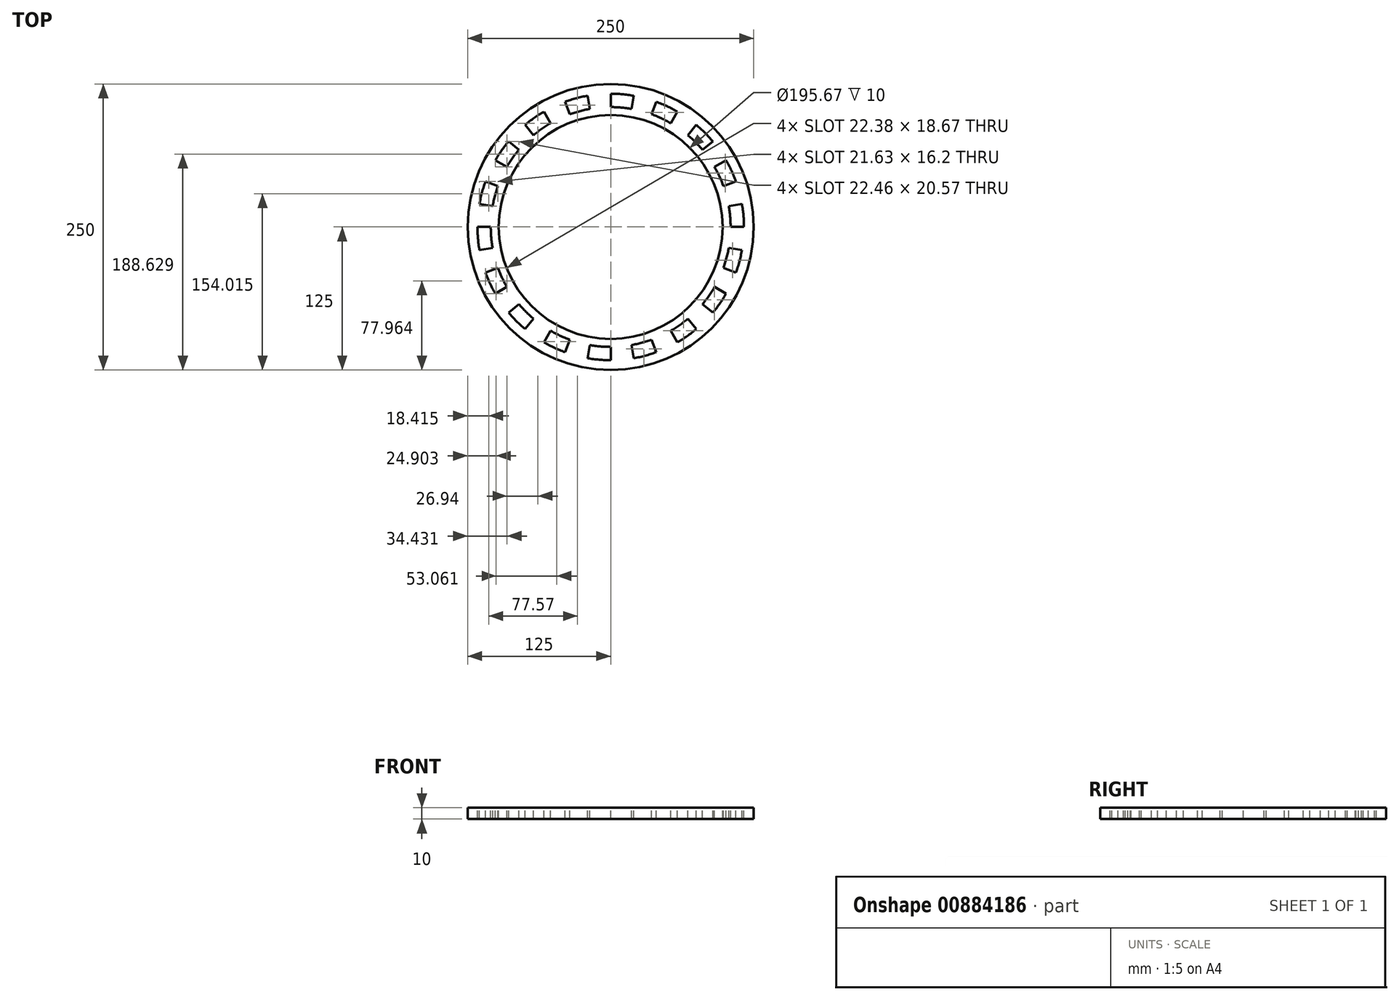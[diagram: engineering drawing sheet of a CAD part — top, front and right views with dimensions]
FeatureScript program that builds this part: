
annotation { "Feature Type Name" : "Feature", "Feature Type Description" : "" }
export const myFeature = defineFeature(function(context is Context, id is Id, definition is map)
    precondition{}
    {
        {
            var Q0;
            Q0=qCreatedBy(makeId("Top.planeOp"),FACE);
            var sketch = newSketch(context, id + "F0", { "sketchPlane" : qUnion([Q0])});
            skCircle(sketch, "E0", {"center": v(0, 0) * mm, "radius": 145 * mm});
            skArc(sketch, "E1", {"start": v(9.54, 136.41) * mm, "mid": v(4.77, 136.66) * mm, "end": v(0, 136.75) * mm});
            skArc(sketch, "E2", {"start": v(8, 114.55) * mm, "mid": v(4, 114.76) * mm, "end": v(0, 114.83) * mm});
            skLineSegment(sketch, "E3", {"start": v(0, 0) * mm, "end": v(0, 38.61) * mm, "construction": true});
            skLineSegment(sketch, "E4", {"start": v(0, 38.61) * mm, "end": v(0, 0) * mm, "construction": true});
            skLineSegment(sketch, "E5", {"start": v(0, 0) * mm, "end": v(-47.77, 0) * mm, "construction": true});
            skLineSegment(sketch, "E6", {"start": v(0, 30) * mm, "end": v(-10, 30) * mm});
            skLineSegment(sketch, "E7", {"start": v(-10, 30) * mm, "end": v(-10, 10) * mm});
            skLineSegment(sketch, "E8", {"start": v(-10, 10) * mm, "end": v(-30, 10) * mm});
            skLineSegment(sketch, "E9", {"start": v(-30, 10) * mm, "end": v(-30, 0) * mm});
            skLineSegment(sketch, "E10.MirrorCS", {"start": v(-30, -10) * mm, "end": v(-30, 0) * mm});
            skLineSegment(sketch, "E11.MirrorCS", {"start": v(-10, -10) * mm, "end": v(-30, -10) * mm});
            skLineSegment(sketch, "E12.MirrorCS", {"start": v(-10, -30) * mm, "end": v(-10, -10) * mm});
            skLineSegment(sketch, "E13.MirrorCS", {"start": v(0, -30) * mm, "end": v(-10, -30) * mm});
            skLineSegment(sketch, "E14.MirrorCS", {"start": v(0, 30) * mm, "end": v(10, 30) * mm});
            skLineSegment(sketch, "E15.MirrorCS", {"start": v(10, 30) * mm, "end": v(10, 10) * mm});
            skLineSegment(sketch, "E16.MirrorCS", {"start": v(10, 10) * mm, "end": v(30, 10) * mm});
            skLineSegment(sketch, "E17.MirrorCS", {"start": v(30, 10) * mm, "end": v(30, 0) * mm});
            skLineSegment(sketch, "E18.MirrorCS", {"start": v(30, -10) * mm, "end": v(30, 0) * mm});
            skLineSegment(sketch, "E19.MirrorCS", {"start": v(10, -10) * mm, "end": v(30, -10) * mm});
            skLineSegment(sketch, "E20.MirrorCS", {"start": v(0, -30) * mm, "end": v(10, -30) * mm});
            skLineSegment(sketch, "E21.MirrorCS", {"start": v(10, -30) * mm, "end": v(10, -10) * mm});
            skLineSegment(sketch, "E22", {"start": v(0, 114.83) * mm, "end": v(0, 136.75) * mm});
            skLineSegment(sketch, "E23", {"start": v(8, 114.55) * mm, "end": v(9.54, 136.41) * mm});
            skArc(sketch, "E24.1.0", {"start": v(-10, 114.4) * mm, "mid": v(-14, 113.98) * mm, "end": v(-17.96, 113.42) * mm});
            skLineSegment(sketch, "E24.1.1", {"start": v(-17.96, 113.42) * mm, "end": v(-21.4, 135.06) * mm});
            skArc(sketch, "E24.1.2", {"start": v(-11.92, 136.23) * mm, "mid": v(-16.67, 135.73) * mm, "end": v(-21.4, 135.06) * mm});
            skLineSegment(sketch, "E24.1.3", {"start": v(-10, 114.4) * mm, "end": v(-11.92, 136.23) * mm});
            skArc(sketch, "E24.2.0", {"start": v(-27.78, 111.42) * mm, "mid": v(-31.65, 110.39) * mm, "end": v(-35.49, 109.21) * mm});
            skLineSegment(sketch, "E24.2.1", {"start": v(-35.49, 109.21) * mm, "end": v(-42.26, 130.05) * mm});
            skArc(sketch, "E24.2.2", {"start": v(-33.08, 132.68) * mm, "mid": v(-37.7, 131.45) * mm, "end": v(-42.26, 130.05) * mm});
            skLineSegment(sketch, "E24.2.3", {"start": v(-27.78, 111.42) * mm, "end": v(-33.08, 132.68) * mm});
            skArc(sketch, "E24.3.0", {"start": v(-44.87, 105.7) * mm, "mid": v(-48.53, 104.07) * mm, "end": v(-52.13, 102.32) * mm});
            skLineSegment(sketch, "E24.3.1", {"start": v(-52.13, 102.32) * mm, "end": v(-62.08, 121.84) * mm});
            skArc(sketch, "E24.3.2", {"start": v(-53.43, 125.88) * mm, "mid": v(-57.8, 123.93) * mm, "end": v(-62.08, 121.84) * mm});
            skLineSegment(sketch, "E24.3.3", {"start": v(-44.87, 105.7) * mm, "end": v(-53.43, 125.88) * mm});
            skArc(sketch, "E24.4.0", {"start": v(-60.85, 97.38) * mm, "mid": v(-64.21, 95.2) * mm, "end": v(-67.5, 92.9) * mm});
            skLineSegment(sketch, "E24.4.1", {"start": v(-67.5, 92.9) * mm, "end": v(-80.38, 110.63) * mm});
            skArc(sketch, "E24.4.2", {"start": v(-72.47, 115.97) * mm, "mid": v(-76.47, 113.37) * mm, "end": v(-80.38, 110.63) * mm});
            skLineSegment(sketch, "E24.4.3", {"start": v(-60.85, 97.38) * mm, "end": v(-72.47, 115.97) * mm});
            skArc(sketch, "E24.5.0", {"start": v(-75.34, 86.67) * mm, "mid": v(-78.32, 83.98) * mm, "end": v(-81.2, 81.2) * mm});
            skLineSegment(sketch, "E24.5.1", {"start": v(-81.2, 81.2) * mm, "end": v(-96.7, 96.7) * mm});
            skArc(sketch, "E24.5.2", {"start": v(-89.71, 103.2) * mm, "mid": v(-93.26, 100.01) * mm, "end": v(-96.7, 96.7) * mm});
            skLineSegment(sketch, "E24.5.3", {"start": v(-75.34, 86.67) * mm, "end": v(-89.71, 103.2) * mm});
            skArc(sketch, "E24.6.0", {"start": v(-87.97, 73.81) * mm, "mid": v(-90.5, 70.7) * mm, "end": v(-92.9, 67.5) * mm});
            skLineSegment(sketch, "E24.6.1", {"start": v(-92.9, 67.5) * mm, "end": v(-110.63, 80.38) * mm});
            skArc(sketch, "E24.6.2", {"start": v(-104.75, 87.9) * mm, "mid": v(-107.76, 84.19) * mm, "end": v(-110.63, 80.38) * mm});
            skLineSegment(sketch, "E24.6.3", {"start": v(-87.97, 73.81) * mm, "end": v(-104.75, 87.9) * mm});
            skArc(sketch, "E24.7.0", {"start": v(-98.43, 59.14) * mm, "mid": v(-100.44, 55.67) * mm, "end": v(-102.32, 52.13) * mm});
            skLineSegment(sketch, "E24.7.1", {"start": v(-102.32, 52.13) * mm, "end": v(-121.84, 62.08) * mm});
            skArc(sketch, "E24.7.2", {"start": v(-117.22, 70.43) * mm, "mid": v(-119.6, 66.3) * mm, "end": v(-121.84, 62.08) * mm});
            skLineSegment(sketch, "E24.7.3", {"start": v(-98.43, 59.14) * mm, "end": v(-117.22, 70.43) * mm});
            skArc(sketch, "E24.8.0", {"start": v(-106.47, 43.02) * mm, "mid": v(-107.9, 39.28) * mm, "end": v(-109.21, 35.49) * mm});
            skLineSegment(sketch, "E24.8.1", {"start": v(-109.21, 35.49) * mm, "end": v(-130.05, 42.26) * mm});
            skArc(sketch, "E24.8.2", {"start": v(-126.79, 51.23) * mm, "mid": v(-128.5, 46.77) * mm, "end": v(-130.05, 42.26) * mm});
            skLineSegment(sketch, "E24.8.3", {"start": v(-106.47, 43.02) * mm, "end": v(-126.79, 51.23) * mm});
            skArc(sketch, "E24.9.0", {"start": v(-111.9, 25.83) * mm, "mid": v(-112.72, 21.91) * mm, "end": v(-113.42, 17.96) * mm});
            skLineSegment(sketch, "E24.9.1", {"start": v(-113.42, 17.96) * mm, "end": v(-135.06, 21.4) * mm});
            skArc(sketch, "E24.9.2", {"start": v(-133.24, 30.76) * mm, "mid": v(-134.23, 26.1) * mm, "end": v(-135.06, 21.4) * mm});
            skLineSegment(sketch, "E24.9.3", {"start": v(-111.9, 25.83) * mm, "end": v(-133.24, 30.76) * mm});
            skArc(sketch, "E24.10.0", {"start": v(-114.55, 8) * mm, "mid": v(-114.76, 4) * mm, "end": v(-114.83, 0) * mm});
            skLineSegment(sketch, "E24.10.1", {"start": v(-114.83, 0) * mm, "end": v(-136.75, 0) * mm});
            skArc(sketch, "E24.10.2", {"start": v(-136.41, 9.54) * mm, "mid": v(-136.66, 4.77) * mm, "end": v(-136.75, 0) * mm});
            skLineSegment(sketch, "E24.10.3", {"start": v(-114.55, 8) * mm, "end": v(-136.41, 9.54) * mm});
            skArc(sketch, "E24.11.0", {"start": v(-114.4, -10) * mm, "mid": v(-113.98, -14) * mm, "end": v(-113.42, -17.96) * mm});
            skLineSegment(sketch, "E24.11.1", {"start": v(-113.42, -17.96) * mm, "end": v(-135.06, -21.4) * mm});
            skArc(sketch, "E24.11.2", {"start": v(-136.23, -11.92) * mm, "mid": v(-135.73, -16.67) * mm, "end": v(-135.06, -21.4) * mm});
            skLineSegment(sketch, "E24.11.3", {"start": v(-114.4, -10) * mm, "end": v(-136.23, -11.92) * mm});
            skArc(sketch, "E24.12.0", {"start": v(-111.42, -27.78) * mm, "mid": v(-110.39, -31.65) * mm, "end": v(-109.21, -35.49) * mm});
            skLineSegment(sketch, "E24.12.1", {"start": v(-109.21, -35.49) * mm, "end": v(-130.05, -42.26) * mm});
            skArc(sketch, "E24.12.2", {"start": v(-132.68, -33.08) * mm, "mid": v(-131.45, -37.7) * mm, "end": v(-130.05, -42.26) * mm});
            skLineSegment(sketch, "E24.12.3", {"start": v(-111.42, -27.78) * mm, "end": v(-132.68, -33.08) * mm});
            skArc(sketch, "E24.13.0", {"start": v(-105.7, -44.87) * mm, "mid": v(-104.07, -48.53) * mm, "end": v(-102.32, -52.13) * mm});
            skLineSegment(sketch, "E24.13.1", {"start": v(-102.32, -52.13) * mm, "end": v(-121.84, -62.08) * mm});
            skArc(sketch, "E24.13.2", {"start": v(-125.88, -53.43) * mm, "mid": v(-123.93, -57.8) * mm, "end": v(-121.84, -62.08) * mm});
            skLineSegment(sketch, "E24.13.3", {"start": v(-105.7, -44.87) * mm, "end": v(-125.88, -53.43) * mm});
            skArc(sketch, "E24.14.0", {"start": v(-97.38, -60.85) * mm, "mid": v(-95.2, -64.21) * mm, "end": v(-92.9, -67.5) * mm});
            skLineSegment(sketch, "E24.14.1", {"start": v(-92.9, -67.5) * mm, "end": v(-110.63, -80.38) * mm});
            skArc(sketch, "E24.14.2", {"start": v(-115.97, -72.47) * mm, "mid": v(-113.37, -76.47) * mm, "end": v(-110.63, -80.38) * mm});
            skLineSegment(sketch, "E24.14.3", {"start": v(-97.38, -60.85) * mm, "end": v(-115.97, -72.47) * mm});
            skArc(sketch, "E24.15.0", {"start": v(-86.67, -75.34) * mm, "mid": v(-83.98, -78.32) * mm, "end": v(-81.2, -81.2) * mm});
            skLineSegment(sketch, "E24.15.1", {"start": v(-81.2, -81.2) * mm, "end": v(-96.7, -96.7) * mm});
            skArc(sketch, "E24.15.2", {"start": v(-103.2, -89.71) * mm, "mid": v(-100.01, -93.26) * mm, "end": v(-96.7, -96.7) * mm});
            skLineSegment(sketch, "E24.15.3", {"start": v(-86.67, -75.34) * mm, "end": v(-103.2, -89.71) * mm});
            skArc(sketch, "E24.16.0", {"start": v(-73.81, -87.97) * mm, "mid": v(-70.7, -90.5) * mm, "end": v(-67.5, -92.9) * mm});
            skLineSegment(sketch, "E24.16.1", {"start": v(-67.5, -92.9) * mm, "end": v(-80.38, -110.63) * mm});
            skArc(sketch, "E24.16.2", {"start": v(-87.9, -104.75) * mm, "mid": v(-84.19, -107.76) * mm, "end": v(-80.38, -110.63) * mm});
            skLineSegment(sketch, "E24.16.3", {"start": v(-73.81, -87.97) * mm, "end": v(-87.9, -104.75) * mm});
            skArc(sketch, "E24.17.0", {"start": v(-59.14, -98.43) * mm, "mid": v(-55.67, -100.44) * mm, "end": v(-52.13, -102.32) * mm});
            skLineSegment(sketch, "E24.17.1", {"start": v(-52.13, -102.32) * mm, "end": v(-62.08, -121.84) * mm});
            skArc(sketch, "E24.17.2", {"start": v(-70.43, -117.22) * mm, "mid": v(-66.3, -119.6) * mm, "end": v(-62.08, -121.84) * mm});
            skLineSegment(sketch, "E24.17.3", {"start": v(-59.14, -98.43) * mm, "end": v(-70.43, -117.22) * mm});
            skArc(sketch, "E24.18.0", {"start": v(-43.02, -106.47) * mm, "mid": v(-39.28, -107.9) * mm, "end": v(-35.49, -109.21) * mm});
            skLineSegment(sketch, "E24.18.1", {"start": v(-35.49, -109.21) * mm, "end": v(-42.26, -130.05) * mm});
            skArc(sketch, "E24.18.2", {"start": v(-51.23, -126.79) * mm, "mid": v(-46.77, -128.5) * mm, "end": v(-42.26, -130.05) * mm});
            skLineSegment(sketch, "E24.18.3", {"start": v(-43.02, -106.47) * mm, "end": v(-51.23, -126.79) * mm});
            skArc(sketch, "E24.19.0", {"start": v(-25.83, -111.9) * mm, "mid": v(-21.91, -112.72) * mm, "end": v(-17.96, -113.42) * mm});
            skLineSegment(sketch, "E24.19.1", {"start": v(-17.96, -113.42) * mm, "end": v(-21.4, -135.06) * mm});
            skArc(sketch, "E24.19.2", {"start": v(-30.76, -133.24) * mm, "mid": v(-26.1, -134.23) * mm, "end": v(-21.4, -135.06) * mm});
            skLineSegment(sketch, "E24.19.3", {"start": v(-25.83, -111.9) * mm, "end": v(-30.76, -133.24) * mm});
            skArc(sketch, "E24.20.0", {"start": v(-8, -114.55) * mm, "mid": v(-4, -114.76) * mm, "end": v(0, -114.83) * mm});
            skLineSegment(sketch, "E24.20.1", {"start": v(0, -114.83) * mm, "end": v(0, -136.75) * mm});
            skArc(sketch, "E24.20.2", {"start": v(-9.54, -136.41) * mm, "mid": v(-4.77, -136.66) * mm, "end": v(0, -136.75) * mm});
            skLineSegment(sketch, "E24.20.3", {"start": v(-8, -114.55) * mm, "end": v(-9.54, -136.41) * mm});
            skArc(sketch, "E24.21.0", {"start": v(10, -114.4) * mm, "mid": v(14, -113.98) * mm, "end": v(17.96, -113.42) * mm});
            skLineSegment(sketch, "E24.21.1", {"start": v(17.96, -113.42) * mm, "end": v(21.4, -135.06) * mm});
            skArc(sketch, "E24.21.2", {"start": v(11.92, -136.23) * mm, "mid": v(16.67, -135.73) * mm, "end": v(21.4, -135.06) * mm});
            skLineSegment(sketch, "E24.21.3", {"start": v(10, -114.4) * mm, "end": v(11.92, -136.23) * mm});
            skArc(sketch, "E24.22.0", {"start": v(27.78, -111.42) * mm, "mid": v(31.65, -110.39) * mm, "end": v(35.49, -109.21) * mm});
            skLineSegment(sketch, "E24.22.1", {"start": v(35.49, -109.21) * mm, "end": v(42.26, -130.05) * mm});
            skArc(sketch, "E24.22.2", {"start": v(33.08, -132.68) * mm, "mid": v(37.7, -131.45) * mm, "end": v(42.26, -130.05) * mm});
            skLineSegment(sketch, "E24.22.3", {"start": v(27.78, -111.42) * mm, "end": v(33.08, -132.68) * mm});
            skArc(sketch, "E24.23.0", {"start": v(44.87, -105.7) * mm, "mid": v(48.53, -104.07) * mm, "end": v(52.13, -102.32) * mm});
            skLineSegment(sketch, "E24.23.1", {"start": v(52.13, -102.32) * mm, "end": v(62.08, -121.84) * mm});
            skArc(sketch, "E24.23.2", {"start": v(53.43, -125.88) * mm, "mid": v(57.8, -123.93) * mm, "end": v(62.08, -121.84) * mm});
            skLineSegment(sketch, "E24.23.3", {"start": v(44.87, -105.7) * mm, "end": v(53.43, -125.88) * mm});
            skArc(sketch, "E24.24.0", {"start": v(60.85, -97.38) * mm, "mid": v(64.21, -95.2) * mm, "end": v(67.5, -92.9) * mm});
            skLineSegment(sketch, "E24.24.1", {"start": v(67.5, -92.9) * mm, "end": v(80.38, -110.63) * mm});
            skArc(sketch, "E24.24.2", {"start": v(72.47, -115.97) * mm, "mid": v(76.47, -113.37) * mm, "end": v(80.38, -110.63) * mm});
            skLineSegment(sketch, "E24.24.3", {"start": v(60.85, -97.38) * mm, "end": v(72.47, -115.97) * mm});
            skArc(sketch, "E24.25.0", {"start": v(75.34, -86.67) * mm, "mid": v(78.32, -83.98) * mm, "end": v(81.2, -81.2) * mm});
            skLineSegment(sketch, "E24.25.1", {"start": v(81.2, -81.2) * mm, "end": v(96.7, -96.7) * mm});
            skArc(sketch, "E24.25.2", {"start": v(89.71, -103.2) * mm, "mid": v(93.26, -100.01) * mm, "end": v(96.7, -96.7) * mm});
            skLineSegment(sketch, "E24.25.3", {"start": v(75.34, -86.67) * mm, "end": v(89.71, -103.2) * mm});
            skArc(sketch, "E24.26.0", {"start": v(87.97, -73.81) * mm, "mid": v(90.5, -70.7) * mm, "end": v(92.9, -67.5) * mm});
            skLineSegment(sketch, "E24.26.1", {"start": v(92.9, -67.5) * mm, "end": v(110.63, -80.38) * mm});
            skArc(sketch, "E24.26.2", {"start": v(104.75, -87.9) * mm, "mid": v(107.76, -84.19) * mm, "end": v(110.63, -80.38) * mm});
            skLineSegment(sketch, "E24.26.3", {"start": v(87.97, -73.81) * mm, "end": v(104.75, -87.9) * mm});
            skArc(sketch, "E24.27.0", {"start": v(98.43, -59.14) * mm, "mid": v(100.44, -55.67) * mm, "end": v(102.32, -52.13) * mm});
            skLineSegment(sketch, "E24.27.1", {"start": v(102.32, -52.13) * mm, "end": v(121.84, -62.08) * mm});
            skArc(sketch, "E24.27.2", {"start": v(117.22, -70.43) * mm, "mid": v(119.6, -66.3) * mm, "end": v(121.84, -62.08) * mm});
            skLineSegment(sketch, "E24.27.3", {"start": v(98.43, -59.14) * mm, "end": v(117.22, -70.43) * mm});
            skArc(sketch, "E24.28.0", {"start": v(106.47, -43.02) * mm, "mid": v(107.9, -39.28) * mm, "end": v(109.21, -35.49) * mm});
            skLineSegment(sketch, "E24.28.1", {"start": v(109.21, -35.49) * mm, "end": v(130.05, -42.26) * mm});
            skArc(sketch, "E24.28.2", {"start": v(126.79, -51.23) * mm, "mid": v(128.5, -46.77) * mm, "end": v(130.05, -42.26) * mm});
            skLineSegment(sketch, "E24.28.3", {"start": v(106.47, -43.02) * mm, "end": v(126.79, -51.23) * mm});
            skArc(sketch, "E24.29.0", {"start": v(111.9, -25.83) * mm, "mid": v(112.72, -21.91) * mm, "end": v(113.42, -17.96) * mm});
            skLineSegment(sketch, "E24.29.1", {"start": v(113.42, -17.96) * mm, "end": v(135.06, -21.4) * mm});
            skArc(sketch, "E24.29.2", {"start": v(133.24, -30.76) * mm, "mid": v(134.23, -26.1) * mm, "end": v(135.06, -21.4) * mm});
            skLineSegment(sketch, "E24.29.3", {"start": v(111.9, -25.83) * mm, "end": v(133.24, -30.76) * mm});
            skArc(sketch, "E24.30.0", {"start": v(114.55, -8) * mm, "mid": v(114.76, -4) * mm, "end": v(114.83, 0) * mm});
            skLineSegment(sketch, "E24.30.1", {"start": v(114.83, 0) * mm, "end": v(136.75, 0) * mm});
            skArc(sketch, "E24.30.2", {"start": v(136.41, -9.54) * mm, "mid": v(136.66, -4.77) * mm, "end": v(136.75, 0) * mm});
            skLineSegment(sketch, "E24.30.3", {"start": v(114.55, -8) * mm, "end": v(136.41, -9.54) * mm});
            skArc(sketch, "E24.31.0", {"start": v(114.4, 10) * mm, "mid": v(113.98, 14) * mm, "end": v(113.42, 17.96) * mm});
            skLineSegment(sketch, "E24.31.1", {"start": v(113.42, 17.96) * mm, "end": v(135.06, 21.4) * mm});
            skArc(sketch, "E24.31.2", {"start": v(136.23, 11.92) * mm, "mid": v(135.73, 16.67) * mm, "end": v(135.06, 21.4) * mm});
            skLineSegment(sketch, "E24.31.3", {"start": v(114.4, 10) * mm, "end": v(136.23, 11.92) * mm});
            skArc(sketch, "E24.32.0", {"start": v(111.42, 27.78) * mm, "mid": v(110.39, 31.65) * mm, "end": v(109.21, 35.49) * mm});
            skLineSegment(sketch, "E24.32.1", {"start": v(109.21, 35.49) * mm, "end": v(130.05, 42.26) * mm});
            skArc(sketch, "E24.32.2", {"start": v(132.68, 33.08) * mm, "mid": v(131.45, 37.7) * mm, "end": v(130.05, 42.26) * mm});
            skLineSegment(sketch, "E24.32.3", {"start": v(111.42, 27.78) * mm, "end": v(132.68, 33.08) * mm});
            skArc(sketch, "E24.33.0", {"start": v(105.7, 44.87) * mm, "mid": v(104.07, 48.53) * mm, "end": v(102.32, 52.13) * mm});
            skLineSegment(sketch, "E24.33.1", {"start": v(102.32, 52.13) * mm, "end": v(121.84, 62.08) * mm});
            skArc(sketch, "E24.33.2", {"start": v(125.88, 53.43) * mm, "mid": v(123.93, 57.8) * mm, "end": v(121.84, 62.08) * mm});
            skLineSegment(sketch, "E24.33.3", {"start": v(105.7, 44.87) * mm, "end": v(125.88, 53.43) * mm});
            skArc(sketch, "E24.34.0", {"start": v(97.38, 60.85) * mm, "mid": v(95.2, 64.21) * mm, "end": v(92.9, 67.5) * mm});
            skLineSegment(sketch, "E24.34.1", {"start": v(92.9, 67.5) * mm, "end": v(110.63, 80.38) * mm});
            skArc(sketch, "E24.34.2", {"start": v(115.97, 72.47) * mm, "mid": v(113.37, 76.47) * mm, "end": v(110.63, 80.38) * mm});
            skLineSegment(sketch, "E24.34.3", {"start": v(97.38, 60.85) * mm, "end": v(115.97, 72.47) * mm});
            skArc(sketch, "E24.35.0", {"start": v(86.67, 75.34) * mm, "mid": v(83.98, 78.32) * mm, "end": v(81.2, 81.2) * mm});
            skLineSegment(sketch, "E24.35.1", {"start": v(81.2, 81.2) * mm, "end": v(96.7, 96.7) * mm});
            skArc(sketch, "E24.35.2", {"start": v(103.2, 89.71) * mm, "mid": v(100.01, 93.26) * mm, "end": v(96.7, 96.7) * mm});
            skLineSegment(sketch, "E24.35.3", {"start": v(86.67, 75.34) * mm, "end": v(103.2, 89.71) * mm});
            skArc(sketch, "E24.36.0", {"start": v(73.81, 87.97) * mm, "mid": v(70.7, 90.5) * mm, "end": v(67.5, 92.9) * mm});
            skLineSegment(sketch, "E24.36.1", {"start": v(67.5, 92.9) * mm, "end": v(80.38, 110.63) * mm});
            skArc(sketch, "E24.36.2", {"start": v(87.9, 104.75) * mm, "mid": v(84.19, 107.76) * mm, "end": v(80.38, 110.63) * mm});
            skLineSegment(sketch, "E24.36.3", {"start": v(73.81, 87.97) * mm, "end": v(87.9, 104.75) * mm});
            skArc(sketch, "E24.37.0", {"start": v(59.14, 98.43) * mm, "mid": v(55.67, 100.44) * mm, "end": v(52.13, 102.32) * mm});
            skLineSegment(sketch, "E24.37.1", {"start": v(52.13, 102.32) * mm, "end": v(62.08, 121.84) * mm});
            skArc(sketch, "E24.37.2", {"start": v(70.43, 117.22) * mm, "mid": v(66.3, 119.6) * mm, "end": v(62.08, 121.84) * mm});
            skLineSegment(sketch, "E24.37.3", {"start": v(59.14, 98.43) * mm, "end": v(70.43, 117.22) * mm});
            skArc(sketch, "E24.38.0", {"start": v(43.02, 106.47) * mm, "mid": v(39.28, 107.9) * mm, "end": v(35.49, 109.21) * mm});
            skLineSegment(sketch, "E24.38.1", {"start": v(35.49, 109.21) * mm, "end": v(42.26, 130.05) * mm});
            skArc(sketch, "E24.38.2", {"start": v(51.23, 126.79) * mm, "mid": v(46.77, 128.5) * mm, "end": v(42.26, 130.05) * mm});
            skLineSegment(sketch, "E24.38.3", {"start": v(43.02, 106.47) * mm, "end": v(51.23, 126.79) * mm});
            skArc(sketch, "E24.39.0", {"start": v(25.83, 111.9) * mm, "mid": v(21.91, 112.72) * mm, "end": v(17.96, 113.42) * mm});
            skLineSegment(sketch, "E24.39.1", {"start": v(17.96, 113.42) * mm, "end": v(21.4, 135.06) * mm});
            skArc(sketch, "E24.39.2", {"start": v(30.76, 133.24) * mm, "mid": v(26.1, 134.23) * mm, "end": v(21.4, 135.06) * mm});
            skLineSegment(sketch, "E24.39.3", {"start": v(25.83, 111.9) * mm, "end": v(30.76, 133.24) * mm});
            skCircle(sketch, "E25", {"center": v(0, 0) * mm, "radius": 50 * mm});
            skSolve(sketch);
        }
        {
            var Q0;
            Q0=makeQuery(id+"F0.imprint","IMPRINT",FACE,{"disambiguationData":[TD([[makeQuery(id+"F0.imprint","IMPRINT",EDGE,{"derivedFrom":sQuery(id+"F0.wireOp",EDGE,"E6")}),-1.0]])]});
            extrude(context, id + "F1", {"entities" : qUnion([Q0]), "depth" : 10 * mm, "offsetDistance" : 25 * mm});
        }
        {
            var Q0;
            Q0=makeQuery(id+"F1.opExtrude","CAP_FACE",FACE,{"disambiguationData":[OSD([sQuery(id+"F0.wireOp",EDGE,"E6"),sQuery(id+"F0.wireOp",EDGE,"E7"),sQuery(id+"F0.wireOp",EDGE,"E8"),sQuery(id+"F0.wireOp",EDGE,"E9"),sQuery(id+"F0.wireOp",EDGE,"E10.MirrorCS"),sQuery(id+"F0.wireOp",EDGE,"E11.MirrorCS"),sQuery(id+"F0.wireOp",EDGE,"E12.MirrorCS"),sQuery(id+"F0.wireOp",EDGE,"E13.MirrorCS"),sQuery(id+"F0.wireOp",EDGE,"E14.MirrorCS"),sQuery(id+"F0.wireOp",EDGE,"E15.MirrorCS"),sQuery(id+"F0.wireOp",EDGE,"E16.MirrorCS"),sQuery(id+"F0.wireOp",EDGE,"E17.MirrorCS"),sQuery(id+"F0.wireOp",EDGE,"E18.MirrorCS"),sQuery(id+"F0.wireOp",EDGE,"E19.MirrorCS"),sQuery(id+"F0.wireOp",EDGE,"E20.MirrorCS"),sQuery(id+"F0.wireOp",EDGE,"E21.MirrorCS"),sQuery(id+"F0.wireOp",EDGE,"E25")])],"isStart":false});
            var sketch = newSketch(context, id + "F2", { "sketchPlane" : qUnion([Q0])});
            skCircle(sketch, "E26", {"center": v(0, 0) * mm, "radius": 125 * mm});
            skCircle(sketch, "E27", {"center": v(0, 0) * mm, "radius": 40.45 * mm});
            skSolve(sketch);
        }
        {
            var Q0;
            Q0=qSketchRegion(id+"F2",true);
            extrude(context, id + "F3", {"entities" : qUnion([Q0]), "operationType" : NewBodyOperationType.ADD, "oppositeDirection" : true, "depth" : 10 * mm, "offsetDistance" : 25 * mm});
        }
        {
            var Q0;
            Q0=makeQuery(id+"F3.boolean.opBoolean","MERGE",FACE,{"derivedFrom":[makeQuery(id+"F1.opExtrude","CAP_FACE",FACE,{"disambiguationData":[OSD([sQuery(id+"F0.wireOp",EDGE,"E6"),sQuery(id+"F0.wireOp",EDGE,"E7"),sQuery(id+"F0.wireOp",EDGE,"E8"),sQuery(id+"F0.wireOp",EDGE,"E9"),sQuery(id+"F0.wireOp",EDGE,"E10.MirrorCS"),sQuery(id+"F0.wireOp",EDGE,"E11.MirrorCS"),sQuery(id+"F0.wireOp",EDGE,"E12.MirrorCS"),sQuery(id+"F0.wireOp",EDGE,"E13.MirrorCS"),sQuery(id+"F0.wireOp",EDGE,"E14.MirrorCS"),sQuery(id+"F0.wireOp",EDGE,"E15.MirrorCS"),sQuery(id+"F0.wireOp",EDGE,"E16.MirrorCS"),sQuery(id+"F0.wireOp",EDGE,"E17.MirrorCS"),sQuery(id+"F0.wireOp",EDGE,"E18.MirrorCS"),sQuery(id+"F0.wireOp",EDGE,"E19.MirrorCS"),sQuery(id+"F0.wireOp",EDGE,"E20.MirrorCS"),sQuery(id+"F0.wireOp",EDGE,"E21.MirrorCS"),sQuery(id+"F0.wireOp",EDGE,"E25")])],"isStart":false}),makeQuery(id+"F3.opExtrude","CAP_FACE",FACE,{"disambiguationData":[OSD([sQuery(id+"F2.wireOp",EDGE,"E26"),sQuery(id+"F2.wireOp",EDGE,"E27")])],"isStart":true})]});
            var sketch = newSketch(context, id + "F4", { "sketchPlane" : qUnion([Q0])});
            skLineSegment(sketch, "E28", {"start": v(0, 104.8) * mm, "end": v(0, 116.46) * mm});
            skLineSegment(sketch, "E29", {"start": v(0, 116.46) * mm, "end": v(0, 104.8) * mm});
            skLineSegment(sketch, "E30", {"start": v(18.2, 103.21) * mm, "end": v(20.22, 114.69) * mm});
            skArc(sketch, "E31", {"start": v(20.22, 114.69) * mm, "mid": v(10.15, 116.01) * mm, "end": v(0, 116.46) * mm});
            skArc(sketch, "E32", {"start": v(18.2, 103.21) * mm, "mid": v(9.13, 104.4) * mm, "end": v(0, 104.8) * mm});
            skArc(sketch, "E33.1.0", {"start": v(-18.2, 103.21) * mm, "mid": v(-27.12, 101.23) * mm, "end": v(-35.84, 98.48) * mm});
            skLineSegment(sketch, "E33.1.1", {"start": v(-39.83, 109.43) * mm, "end": v(-35.84, 98.48) * mm});
            skArc(sketch, "E33.1.2", {"start": v(-20.22, 114.69) * mm, "mid": v(-30.14, 112.49) * mm, "end": v(-39.83, 109.43) * mm});
            skLineSegment(sketch, "E33.1.3", {"start": v(-18.2, 103.21) * mm, "end": v(-20.22, 114.69) * mm});
            skArc(sketch, "E33.2.0", {"start": v(-52.4, 90.76) * mm, "mid": v(-60.11, 85.85) * mm, "end": v(-67.37, 80.28) * mm});
            skLineSegment(sketch, "E33.2.1", {"start": v(-74.86, 89.21) * mm, "end": v(-67.37, 80.28) * mm});
            skArc(sketch, "E33.2.2", {"start": v(-58.23, 100.85) * mm, "mid": v(-66.8, 95.4) * mm, "end": v(-74.86, 89.21) * mm});
            skLineSegment(sketch, "E33.2.3", {"start": v(-52.4, 90.76) * mm, "end": v(-58.23, 100.85) * mm});
            skArc(sketch, "E33.3.0", {"start": v(-80.28, 67.37) * mm, "mid": v(-85.85, 60.11) * mm, "end": v(-90.76, 52.4) * mm});
            skLineSegment(sketch, "E33.3.1", {"start": v(-100.85, 58.23) * mm, "end": v(-90.76, 52.4) * mm});
            skArc(sketch, "E33.3.2", {"start": v(-89.21, 74.86) * mm, "mid": v(-95.4, 66.8) * mm, "end": v(-100.85, 58.23) * mm});
            skLineSegment(sketch, "E33.3.3", {"start": v(-80.28, 67.37) * mm, "end": v(-89.21, 74.86) * mm});
            skArc(sketch, "E33.4.0", {"start": v(-98.48, 35.84) * mm, "mid": v(-101.23, 27.12) * mm, "end": v(-103.21, 18.2) * mm});
            skLineSegment(sketch, "E33.4.1", {"start": v(-114.69, 20.22) * mm, "end": v(-103.21, 18.2) * mm});
            skArc(sketch, "E33.4.2", {"start": v(-109.43, 39.83) * mm, "mid": v(-112.49, 30.14) * mm, "end": v(-114.69, 20.22) * mm});
            skLineSegment(sketch, "E33.4.3", {"start": v(-98.48, 35.84) * mm, "end": v(-109.43, 39.83) * mm});
            skArc(sketch, "E33.5.0", {"start": v(-104.8, 0) * mm, "mid": v(-104.4, -9.13) * mm, "end": v(-103.21, -18.2) * mm});
            skLineSegment(sketch, "E33.5.1", {"start": v(-114.69, -20.22) * mm, "end": v(-103.21, -18.2) * mm});
            skArc(sketch, "E33.5.2", {"start": v(-116.46, 0) * mm, "mid": v(-116.01, -10.15) * mm, "end": v(-114.69, -20.22) * mm});
            skLineSegment(sketch, "E33.5.3", {"start": v(-104.8, 0) * mm, "end": v(-116.46, 0) * mm});
            skArc(sketch, "E33.6.0", {"start": v(-98.48, -35.84) * mm, "mid": v(-94.98, -44.3) * mm, "end": v(-90.76, -52.4) * mm});
            skLineSegment(sketch, "E33.6.1", {"start": v(-100.85, -58.23) * mm, "end": v(-90.76, -52.4) * mm});
            skArc(sketch, "E33.6.2", {"start": v(-109.43, -39.83) * mm, "mid": v(-105.55, -49.22) * mm, "end": v(-100.85, -58.23) * mm});
            skLineSegment(sketch, "E33.6.3", {"start": v(-98.48, -35.84) * mm, "end": v(-109.43, -39.83) * mm});
            skArc(sketch, "E33.7.0", {"start": v(-80.28, -67.37) * mm, "mid": v(-74.1, -74.1) * mm, "end": v(-67.37, -80.28) * mm});
            skLineSegment(sketch, "E33.7.1", {"start": v(-74.86, -89.21) * mm, "end": v(-67.37, -80.28) * mm});
            skArc(sketch, "E33.7.2", {"start": v(-89.21, -74.86) * mm, "mid": v(-82.35, -82.35) * mm, "end": v(-74.86, -89.21) * mm});
            skLineSegment(sketch, "E33.7.3", {"start": v(-80.28, -67.37) * mm, "end": v(-89.21, -74.86) * mm});
            skArc(sketch, "E33.8.0", {"start": v(-52.4, -90.76) * mm, "mid": v(-44.3, -94.98) * mm, "end": v(-35.84, -98.48) * mm});
            skLineSegment(sketch, "E33.8.1", {"start": v(-39.83, -109.43) * mm, "end": v(-35.84, -98.48) * mm});
            skArc(sketch, "E33.8.2", {"start": v(-58.23, -100.85) * mm, "mid": v(-49.22, -105.55) * mm, "end": v(-39.83, -109.43) * mm});
            skLineSegment(sketch, "E33.8.3", {"start": v(-52.4, -90.76) * mm, "end": v(-58.23, -100.85) * mm});
            skArc(sketch, "E33.9.0", {"start": v(-18.2, -103.21) * mm, "mid": v(-9.13, -104.4) * mm, "end": v(0, -104.8) * mm});
            skLineSegment(sketch, "E33.9.1", {"start": v(0, -116.46) * mm, "end": v(0, -104.8) * mm});
            skArc(sketch, "E33.9.2", {"start": v(-20.22, -114.69) * mm, "mid": v(-10.15, -116.01) * mm, "end": v(0, -116.46) * mm});
            skLineSegment(sketch, "E33.9.3", {"start": v(-18.2, -103.21) * mm, "end": v(-20.22, -114.69) * mm});
            skArc(sketch, "E33.10.0", {"start": v(18.2, -103.21) * mm, "mid": v(27.12, -101.23) * mm, "end": v(35.84, -98.48) * mm});
            skLineSegment(sketch, "E33.10.1", {"start": v(39.83, -109.43) * mm, "end": v(35.84, -98.48) * mm});
            skArc(sketch, "E33.10.2", {"start": v(20.22, -114.69) * mm, "mid": v(30.14, -112.49) * mm, "end": v(39.83, -109.43) * mm});
            skLineSegment(sketch, "E33.10.3", {"start": v(18.2, -103.21) * mm, "end": v(20.22, -114.69) * mm});
            skArc(sketch, "E33.11.0", {"start": v(52.4, -90.76) * mm, "mid": v(60.11, -85.85) * mm, "end": v(67.37, -80.28) * mm});
            skLineSegment(sketch, "E33.11.1", {"start": v(74.86, -89.21) * mm, "end": v(67.37, -80.28) * mm});
            skArc(sketch, "E33.11.2", {"start": v(58.23, -100.85) * mm, "mid": v(66.8, -95.4) * mm, "end": v(74.86, -89.21) * mm});
            skLineSegment(sketch, "E33.11.3", {"start": v(52.4, -90.76) * mm, "end": v(58.23, -100.85) * mm});
            skArc(sketch, "E33.12.0", {"start": v(80.28, -67.37) * mm, "mid": v(85.85, -60.11) * mm, "end": v(90.76, -52.4) * mm});
            skLineSegment(sketch, "E33.12.1", {"start": v(100.85, -58.23) * mm, "end": v(90.76, -52.4) * mm});
            skArc(sketch, "E33.12.2", {"start": v(89.21, -74.86) * mm, "mid": v(95.4, -66.8) * mm, "end": v(100.85, -58.23) * mm});
            skLineSegment(sketch, "E33.12.3", {"start": v(80.28, -67.37) * mm, "end": v(89.21, -74.86) * mm});
            skArc(sketch, "E33.13.0", {"start": v(98.48, -35.84) * mm, "mid": v(101.23, -27.12) * mm, "end": v(103.21, -18.2) * mm});
            skLineSegment(sketch, "E33.13.1", {"start": v(114.69, -20.22) * mm, "end": v(103.21, -18.2) * mm});
            skArc(sketch, "E33.13.2", {"start": v(109.43, -39.83) * mm, "mid": v(112.49, -30.14) * mm, "end": v(114.69, -20.22) * mm});
            skLineSegment(sketch, "E33.13.3", {"start": v(98.48, -35.84) * mm, "end": v(109.43, -39.83) * mm});
            skArc(sketch, "E33.14.0", {"start": v(104.8, 0) * mm, "mid": v(104.4, 9.13) * mm, "end": v(103.21, 18.2) * mm});
            skLineSegment(sketch, "E33.14.1", {"start": v(114.69, 20.22) * mm, "end": v(103.21, 18.2) * mm});
            skArc(sketch, "E33.14.2", {"start": v(116.46, 0) * mm, "mid": v(116.01, 10.15) * mm, "end": v(114.69, 20.22) * mm});
            skLineSegment(sketch, "E33.14.3", {"start": v(104.8, 0) * mm, "end": v(116.46, 0) * mm});
            skArc(sketch, "E33.15.0", {"start": v(98.48, 35.84) * mm, "mid": v(94.98, 44.3) * mm, "end": v(90.76, 52.4) * mm});
            skLineSegment(sketch, "E33.15.1", {"start": v(100.85, 58.23) * mm, "end": v(90.76, 52.4) * mm});
            skArc(sketch, "E33.15.2", {"start": v(109.43, 39.83) * mm, "mid": v(105.55, 49.22) * mm, "end": v(100.85, 58.23) * mm});
            skLineSegment(sketch, "E33.15.3", {"start": v(98.48, 35.84) * mm, "end": v(109.43, 39.83) * mm});
            skArc(sketch, "E33.16.0", {"start": v(80.28, 67.37) * mm, "mid": v(74.1, 74.1) * mm, "end": v(67.37, 80.28) * mm});
            skLineSegment(sketch, "E33.16.1", {"start": v(74.86, 89.21) * mm, "end": v(67.37, 80.28) * mm});
            skArc(sketch, "E33.16.2", {"start": v(89.21, 74.86) * mm, "mid": v(82.35, 82.35) * mm, "end": v(74.86, 89.21) * mm});
            skLineSegment(sketch, "E33.16.3", {"start": v(80.28, 67.37) * mm, "end": v(89.21, 74.86) * mm});
            skArc(sketch, "E33.17.0", {"start": v(52.4, 90.76) * mm, "mid": v(44.3, 94.98) * mm, "end": v(35.84, 98.48) * mm});
            skLineSegment(sketch, "E33.17.1", {"start": v(39.83, 109.43) * mm, "end": v(35.84, 98.48) * mm});
            skArc(sketch, "E33.17.2", {"start": v(58.23, 100.85) * mm, "mid": v(49.22, 105.55) * mm, "end": v(39.83, 109.43) * mm});
            skLineSegment(sketch, "E33.17.3", {"start": v(52.4, 90.76) * mm, "end": v(58.23, 100.85) * mm});
            skSolve(sketch);
        }
        {
            var Q0;
            Q0=qSketchRegion(id+"F4",true);
            extrude(context, id + "F5", {"entities" : qUnion([Q0]), "operationType" : NewBodyOperationType.REMOVE, "oppositeDirection" : true, "depth" : 25 * mm, "offsetDistance" : 25 * mm});
        }
        {
            var Q0;
            Q0=makeQuery(id+"F3.boolean.opBoolean","MERGE",FACE,{"derivedFrom":[makeQuery(id+"F1.opExtrude","CAP_FACE",FACE,{"disambiguationData":[OSD([sQuery(id+"F0.wireOp",EDGE,"E6"),sQuery(id+"F0.wireOp",EDGE,"E7"),sQuery(id+"F0.wireOp",EDGE,"E8"),sQuery(id+"F0.wireOp",EDGE,"E9"),sQuery(id+"F0.wireOp",EDGE,"E10.MirrorCS"),sQuery(id+"F0.wireOp",EDGE,"E11.MirrorCS"),sQuery(id+"F0.wireOp",EDGE,"E12.MirrorCS"),sQuery(id+"F0.wireOp",EDGE,"E13.MirrorCS"),sQuery(id+"F0.wireOp",EDGE,"E14.MirrorCS"),sQuery(id+"F0.wireOp",EDGE,"E15.MirrorCS"),sQuery(id+"F0.wireOp",EDGE,"E16.MirrorCS"),sQuery(id+"F0.wireOp",EDGE,"E17.MirrorCS"),sQuery(id+"F0.wireOp",EDGE,"E18.MirrorCS"),sQuery(id+"F0.wireOp",EDGE,"E19.MirrorCS"),sQuery(id+"F0.wireOp",EDGE,"E20.MirrorCS"),sQuery(id+"F0.wireOp",EDGE,"E21.MirrorCS"),sQuery(id+"F0.wireOp",EDGE,"E25")])],"isStart":false}),makeQuery(id+"F3.opExtrude","CAP_FACE",FACE,{"disambiguationData":[OSD([sQuery(id+"F2.wireOp",EDGE,"E26"),sQuery(id+"F2.wireOp",EDGE,"E27")])],"isStart":true})]});
            var sketch = newSketch(context, id + "F6", { "sketchPlane" : qUnion([Q0])});
            skCircle(sketch, "E34", {"center": v(0, 0) * mm, "radius": 97.83 * mm});
            skSolve(sketch);
        }
        {
            var Q0;
            Q0 = qSketchRegion(id + "F6", true);
            extrude(context, id + "F7", {"entities" : qUnion([Q0]), "operationType" : NewBodyOperationType.REMOVE, "oppositeDirection" : true, "depth" : 25 * mm, "offsetDistance" : 25 * mm});
        }
    });
